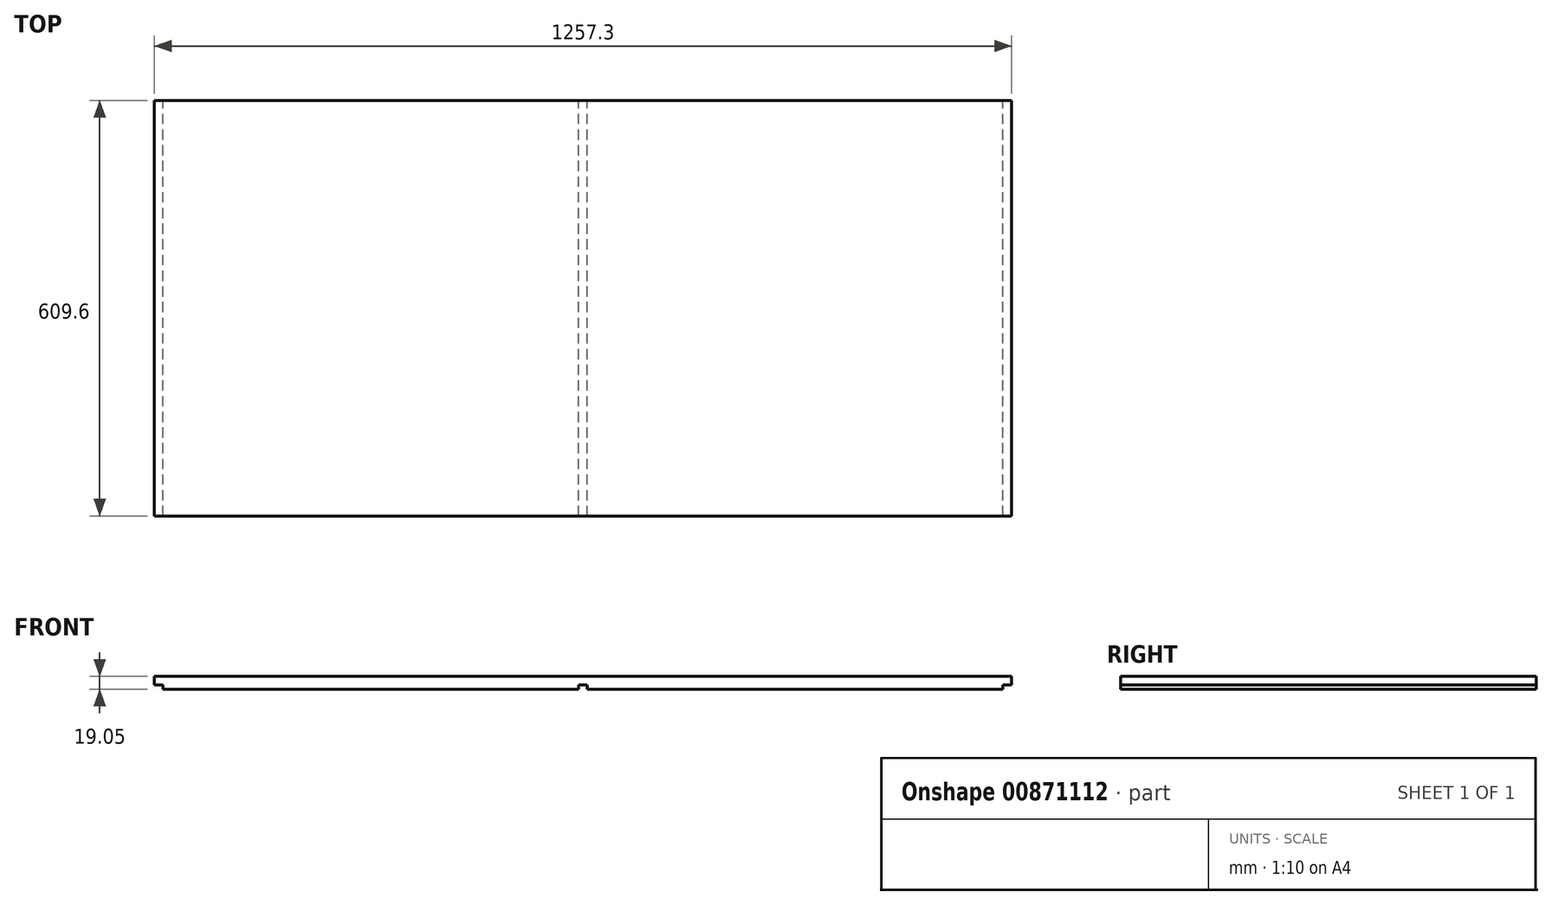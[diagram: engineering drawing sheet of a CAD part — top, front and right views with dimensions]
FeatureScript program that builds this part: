
annotation { "Feature Type Name" : "Feature", "Feature Type Description" : "" }
export const myFeature = defineFeature(function(context is Context, id is Id, definition is map)
    precondition{}
    {
        {
            var Q0;
            Q0=qCreatedBy(makeId("Front.planeOp"),FACE);
            var sketch = newSketch(context, id + "F0", { "sketchPlane" : qUnion([Q0])});
            skLineSegment(sketch, "E0.bottom", {"start": v(12.7, 0) * mm, "end": v(622.3, 0) * mm});
            skLineSegment(sketch, "E0.top", {"start": v(0, 19.05) * mm, "end": v(1257.3, 19.05) * mm});
            skLineSegment(sketch, "E0.left", {"start": v(0, 6.35) * mm, "end": v(0, 19.05) * mm});
            skLineSegment(sketch, "E0.right", {"start": v(1257.3, 6.35) * mm, "end": v(1257.3, 19.05) * mm});
            skLineSegment(sketch, "E1.top", {"start": v(0, 6.35) * mm, "end": v(12.7, 6.35) * mm});
            skLineSegment(sketch, "E1.right", {"start": v(12.7, 0) * mm, "end": v(12.7, 6.35) * mm});
            skLineSegment(sketch, "E2.top", {"start": v(622.3, 6.35) * mm, "end": v(635, 6.35) * mm});
            skLineSegment(sketch, "E2.left", {"start": v(622.3, 0) * mm, "end": v(622.3, 6.35) * mm});
            skLineSegment(sketch, "E2.right", {"start": v(635, 0) * mm, "end": v(635, 6.35) * mm});
            skLineSegment(sketch, "E3.trimOffspring", {"start": v(635, 0) * mm, "end": v(1244.6, 0) * mm});
            skLineSegment(sketch, "E4.top", {"start": v(1257.3, 6.35) * mm, "end": v(1244.6, 6.35) * mm});
            skLineSegment(sketch, "E4.right", {"start": v(1244.6, 0) * mm, "end": v(1244.6, 6.35) * mm});
            skSolve(sketch);
        }
        {
            var Q0;
            Q0 = qSketchRegion(id + "F0", true);
            extrude(context, id + "F1", {"entities" : qUnion([Q0]), "depth" : 609.6 * mm, "offsetDistance" : 25.4 * mm});
        }
    });
